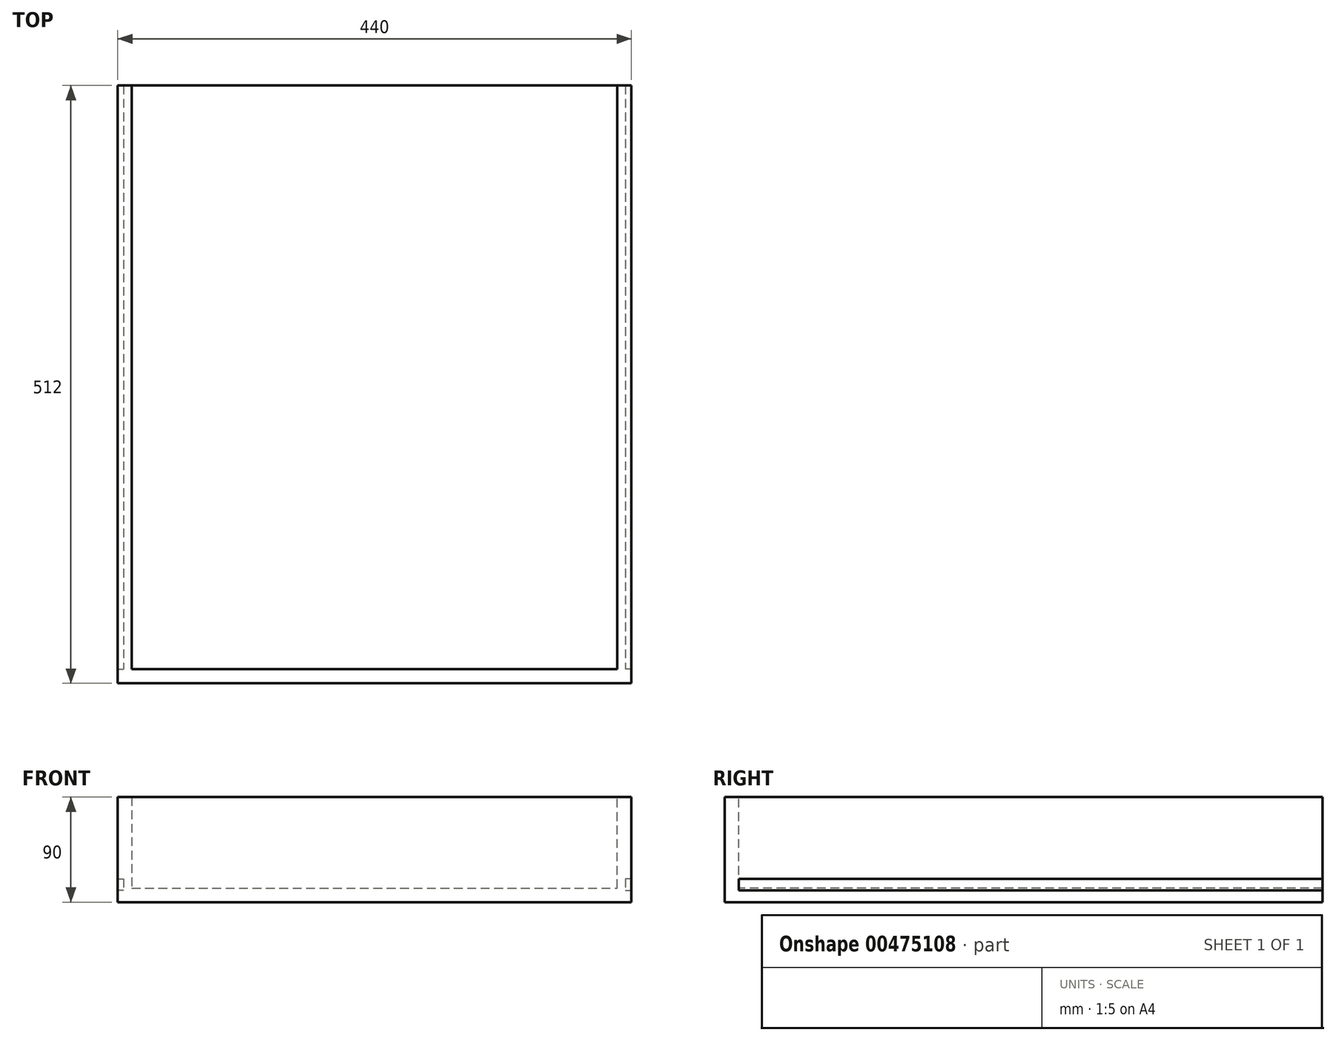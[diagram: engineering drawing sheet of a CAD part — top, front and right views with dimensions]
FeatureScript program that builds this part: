
annotation { "Feature Type Name" : "Feature", "Feature Type Description" : "" }
export const myFeature = defineFeature(function(context is Context, id is Id, definition is map)
    precondition{}
    {
        {
            var Q0;
            Q0=qCreatedBy(makeId("Front.planeOp"),FACE);
            var sketch = newSketch(context, id + "F0", { "sketchPlane" : qUnion([Q0])});
            skLineSegment(sketch, "E0.bottom", {"start": v(-220, 90) * mm, "end": v(220, 90) * mm, "construction": true});
            skLineSegment(sketch, "E0.top", {"start": v(-220, 0) * mm, "end": v(220, 0) * mm, "construction": true});
            skLineSegment(sketch, "E0.left", {"start": v(-220, 90) * mm, "end": v(-220, 0) * mm, "construction": true});
            skLineSegment(sketch, "E0.right", {"start": v(220, 90) * mm, "end": v(220, 0) * mm, "construction": true});
            skLineSegment(sketch, "E1", {"start": v(-220, 12) * mm, "end": v(220, 12) * mm, "construction": true});
            skLineSegment(sketch, "E2", {"start": v(-215, 90) * mm, "end": v(-215, 0) * mm, "construction": true});
            skLineSegment(sketch, "E3", {"start": v(215, 90) * mm, "end": v(215, 0) * mm, "construction": true});
            skLineSegment(sketch, "E4", {"start": v(208, 90) * mm, "end": v(208, 0) * mm, "construction": true});
            skLineSegment(sketch, "E5", {"start": v(-220, 10) * mm, "end": v(220, 10) * mm, "construction": true});
            skLineSegment(sketch, "E6", {"start": v(-220, 20) * mm, "end": v(220, 20) * mm, "construction": true});
            skLineSegment(sketch, "E7", {"start": v(-208, 12) * mm, "end": v(208, 12) * mm});
            skLineSegment(sketch, "E8", {"start": v(220, 0) * mm, "end": v(-220, 0) * mm});
            skLineSegment(sketch, "E9", {"start": v(-220, 90) * mm, "end": v(-220, 20) * mm});
            skLineSegment(sketch, "E10", {"start": v(-215, 20) * mm, "end": v(-215, 10) * mm});
            skLineSegment(sketch, "E11", {"start": v(-215, 10) * mm, "end": v(-220, 10) * mm});
            skLineSegment(sketch, "E12", {"start": v(-220, 20) * mm, "end": v(-215, 20) * mm});
            skLineSegment(sketch, "E13", {"start": v(-220, 10) * mm, "end": v(-220, 0) * mm});
            skLineSegment(sketch, "E14", {"start": v(-220, 90) * mm, "end": v(-208, 90) * mm});
            skLineSegment(sketch, "E15", {"start": v(208, 12) * mm, "end": v(208, 90) * mm});
            skLineSegment(sketch, "E16", {"start": v(208, 90) * mm, "end": v(220, 90) * mm});
            skLineSegment(sketch, "E17", {"start": v(220, 90) * mm, "end": v(220, 20) * mm});
            skLineSegment(sketch, "E18", {"start": v(220, 20) * mm, "end": v(215, 20) * mm});
            skLineSegment(sketch, "E19", {"start": v(215, 10) * mm, "end": v(220, 10) * mm});
            skLineSegment(sketch, "E20", {"start": v(215, 20) * mm, "end": v(215, 10) * mm});
            skLineSegment(sketch, "E21", {"start": v(220, 10) * mm, "end": v(220, 0) * mm});
            skLineSegment(sketch, "E22", {"start": v(-208, 0) * mm, "end": v(-208, 90) * mm, "construction": true});
            skLineSegment(sketch, "E23", {"start": v(-208, 90) * mm, "end": v(-208, 12) * mm});
            skSolve(sketch);
        }
        {
            var Q0;
            Q0=qSketchRegion(id+"F0",true);
            extrude(context, id + "F1", {"entities" : qUnion([Q0]), "oppositeDirection" : true, "depth" : 500 * mm});
        }
        {
            var Q0;
            Q0=qCreatedBy(makeId("Front.planeOp"),FACE);
            var sketch = newSketch(context, id + "F2", { "sketchPlane" : qUnion([Q0])});
            skLineSegment(sketch, "E24.bottom", {"start": v(-220, 90) * mm, "end": v(220, 90) * mm});
            skLineSegment(sketch, "E24.top", {"start": v(-220, 0) * mm, "end": v(220, 0) * mm});
            skLineSegment(sketch, "E24.left", {"start": v(-220, 90) * mm, "end": v(-220, 0) * mm});
            skLineSegment(sketch, "E24.right", {"start": v(220, 90) * mm, "end": v(220, 0) * mm});
            skSolve(sketch);
        }
        {
            var Q0;
            Q0=qSketchRegion(id+"F2",true);
            extrude(context, id + "F3", {"entities" : qUnion([Q0]), "operationType" : NewBodyOperationType.ADD, "depth" : 12 * mm});
        }
    });
